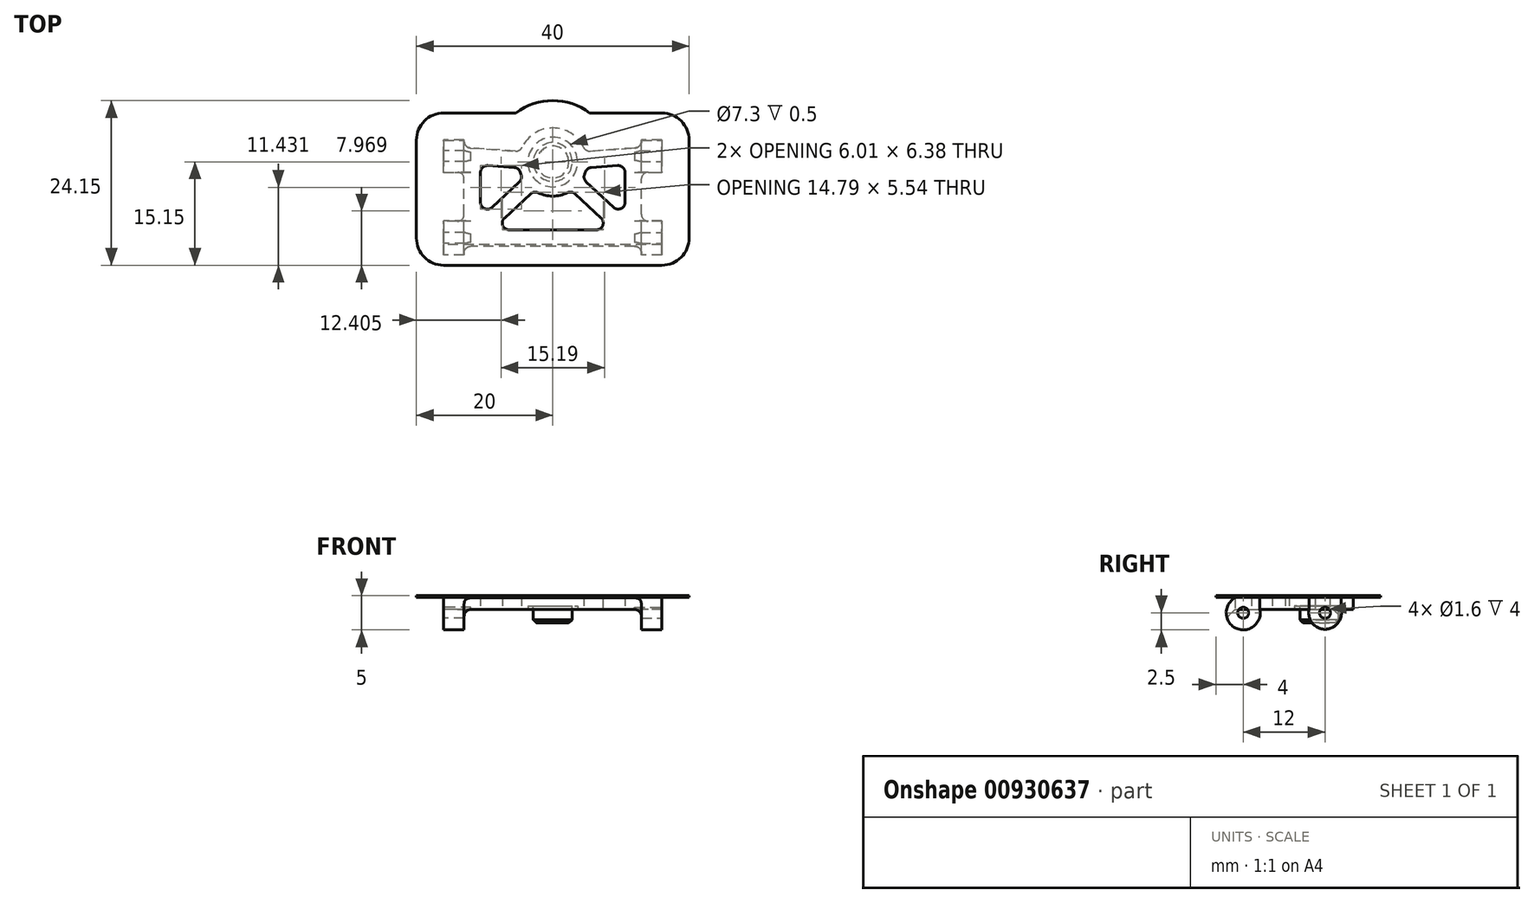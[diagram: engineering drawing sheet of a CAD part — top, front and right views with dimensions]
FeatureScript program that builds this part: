
annotation { "Feature Type Name" : "Feature", "Feature Type Description" : "" }
export const myFeature = defineFeature(function(context is Context, id is Id, definition is map)
    precondition{}
    {
        {
            var Q0;
            Q0=qCreatedBy(makeId("Right.planeOp"),FACE);
            var sketch = newSketch(context, id + "F0", { "sketchPlane" : qUnion([Q0])});
            skArc(sketch, "E0", {"start": v(0, 2.5) * mm, "mid": v(-1.58, -1.94) * mm, "end": v(2.45, 0.5) * mm});
            skArc(sketch, "E1", {"start": v(9.65, 0.5) * mm, "mid": v(12, -2.4) * mm, "end": v(14.35, 0.5) * mm});
            skLineSegment(sketch, "E2", {"start": v(2.45, 0.5) * mm, "end": v(9.65, 0.5) * mm});
            skLineSegment(sketch, "E3", {"start": v(16.35, 2.5) * mm, "end": v(16.35, 0.5) * mm});
            skLineSegment(sketch, "E4", {"start": v(16.35, 0.5) * mm, "end": v(14.35, 0.5) * mm});
            skLineSegment(sketch, "E5", {"start": v(16.35, 2.5) * mm, "end": v(0, 2.5) * mm});
            skSolve(sketch);
        }
        {
            var Q0;
            Q0=qSketchRegion(id+"F0",true);
            extrude(context, id + "F1", {"entities" : qUnion([Q0]), "depth" : 32 * mm, "offsetDistance" : 25 * mm});
        }
        {
            var Q0;
            Q0=makeQuery(id+"F1.opExtrude","SWEPT_FACE",FACE,{"disambiguationData":[OSD([sQuery(id+"F0.wireOp",EDGE,"E3")])]});
            var sketch = newSketch(context, id + "F2", { "sketchPlane" : qUnion([Q0])});
            skLineSegment(sketch, "E6.bottom", {"start": v(-29, 0.5) * mm, "end": v(-3, 0.5) * mm});
            skLineSegment(sketch, "E6.top", {"start": v(-29, -2.5) * mm, "end": v(-3, -2.5) * mm});
            skLineSegment(sketch, "E6.left", {"start": v(-29, 0.5) * mm, "end": v(-29, -2.5) * mm});
            skLineSegment(sketch, "E6.right", {"start": v(-3, 0.5) * mm, "end": v(-3, -2.5) * mm});
            skSolve(sketch);
        }
        {
            var Q0;
            Q0=qSketchRegion(id+"F2",true);
            extrude(context, id + "F3", {"entities" : qUnion([Q0]), "operationType" : NewBodyOperationType.REMOVE, "endBound" : BoundingType.THROUGH_ALL, "oppositeDirection" : true, "depth" : 25 * mm, "offsetDistance" : 25 * mm});
        }
        {
            var Q0;
            Q0=makeQuery(id+"F1.opExtrude","CAP_FACE",FACE,{"disambiguationData":[OSD([sQuery(id+"F0.wireOp",EDGE,"E0"),sQuery(id+"F0.wireOp",EDGE,"E1"),sQuery(id+"F0.wireOp",EDGE,"E2"),sQuery(id+"F0.wireOp",EDGE,"E3"),sQuery(id+"F0.wireOp",EDGE,"E4"),sQuery(id+"F0.wireOp",EDGE,"E5")])],"isStart":false});
            var sketch = newSketch(context, id + "F4", { "sketchPlane" : qUnion([Q0])});
            skCircle(sketch, "E7", {"center": v(0, 0) * mm, "radius": 0.8 * mm});
            skCircle(sketch, "E8", {"center": v(12, 0) * mm, "radius": 0.8 * mm});
            skSolve(sketch);
        }
        {
            var Q0;
            Q0=qSketchRegion(id+"F4",true);
            extrude(context, id + "F5", {"entities" : qUnion([Q0]), "operationType" : NewBodyOperationType.REMOVE, "oppositeDirection" : true, "depth" : 4 * mm, "offsetDistance" : 25 * mm});
        }
        {
            var Q0;
            Q0=makeQuery(id+"F1.opExtrude","CAP_FACE",FACE,{"disambiguationData":[OSD([sQuery(id+"F0.wireOp",EDGE,"E0"),sQuery(id+"F0.wireOp",EDGE,"E1"),sQuery(id+"F0.wireOp",EDGE,"E2"),sQuery(id+"F0.wireOp",EDGE,"E3"),sQuery(id+"F0.wireOp",EDGE,"E4"),sQuery(id+"F0.wireOp",EDGE,"E5")])],"isStart":true});
            var sketch = newSketch(context, id + "F6", { "sketchPlane" : qUnion([Q0])});
            skCircle(sketch, "E9", {"center": v(0, 0) * mm, "radius": 0.8 * mm});
            skCircle(sketch, "E10", {"center": v(-12, 0) * mm, "radius": 0.8 * mm});
            skSolve(sketch);
        }
        {
            var Q0;
            Q0=qSketchRegion(id+"F6",true);
            extrude(context, id + "F7", {"entities" : qUnion([Q0]), "operationType" : NewBodyOperationType.REMOVE, "oppositeDirection" : true, "depth" : 4 * mm, "offsetDistance" : 25 * mm});
        }
        {
            var Q0;
            Q0=makeQuery(id+"F3.boolean.opBoolean","MERGE",FACE,{"derivedFrom":[makeQuery(id+"F1.opExtrude","SWEPT_FACE",FACE,{"disambiguationData":[OSD([sQuery(id+"F0.wireOp",EDGE,"E2")])]}),makeQuery(id+"F1.opExtrude","SWEPT_FACE",FACE,{"disambiguationData":[OSD([sQuery(id+"F0.wireOp",EDGE,"E4")])]}),makeQuery(id+"F3.opExtrude","SWEPT_FACE",FACE,{"disambiguationData":[OSD([sQuery(id+"F2.wireOp",EDGE,"E6.bottom")])]})]});
            var sketch = newSketch(context, id + "F8", { "sketchPlane" : qUnion([Q0])});
            skLineSegment(sketch, "E11", {"start": v(16, 2.45) * mm, "end": v(16, -16.35) * mm, "construction": true});
            skCircle(sketch, "E12", {"center": v(16, -11.15) * mm, "radius": 2.85 * mm});
            skSolve(sketch);
        }
        {
            var Q0;
            Q0=qSketchRegion(id+"F8",true);
            extrude(context, id + "F9", {"entities" : qUnion([Q0]), "operationType" : NewBodyOperationType.ADD, "depth" : 2 * mm, "offsetDistance" : 25 * mm});
        }
        {
            var Q0;
            Q0=makeQuery(id+"F3.boolean.opBoolean","MERGE",FACE,{"derivedFrom":[makeQuery(id+"F1.opExtrude","SWEPT_FACE",FACE,{"disambiguationData":[OSD([sQuery(id+"F0.wireOp",EDGE,"E2")])]}),makeQuery(id+"F1.opExtrude","SWEPT_FACE",FACE,{"disambiguationData":[OSD([sQuery(id+"F0.wireOp",EDGE,"E4")])]}),makeQuery(id+"F3.opExtrude","SWEPT_FACE",FACE,{"disambiguationData":[OSD([sQuery(id+"F2.wireOp",EDGE,"E6.bottom")])]})]});
            var sketch = newSketch(context, id + "F10", { "sketchPlane" : qUnion([Q0])});
            skArc(sketch, "E13", {"start": v(18.74, -6.97) * mm, "mid": v(16, -6.15) * mm, "end": v(13.26, -6.97) * mm});
            skLineSegment(sketch, "E14.bottom", {"start": v(0, -2.45) * mm, "end": v(3, -2.45) * mm});
            skLineSegment(sketch, "E14.top", {"start": v(0, -9.65) * mm, "end": v(3, -9.65) * mm});
            skLineSegment(sketch, "E14.left", {"start": v(0, -2.45) * mm, "end": v(0, -9.65) * mm});
            skLineSegment(sketch, "E14.right", {"start": v(3, -2.45) * mm, "end": v(3, -9.65) * mm});
            skLineSegment(sketch, "E15.bottom", {"start": v(29, -2.45) * mm, "end": v(32, -2.45) * mm});
            skLineSegment(sketch, "E15.top", {"start": v(29, -9.65) * mm, "end": v(32, -9.65) * mm});
            skLineSegment(sketch, "E15.left", {"start": v(29, -2.45) * mm, "end": v(29, -9.65) * mm});
            skLineSegment(sketch, "E15.right", {"start": v(32, -2.45) * mm, "end": v(32, -9.65) * mm});
            skLineSegment(sketch, "E16.bottom", {"start": v(0, -14.35) * mm, "end": v(3, -14.35) * mm});
            skLineSegment(sketch, "E16.left", {"start": v(0, -14.35) * mm, "end": v(0, -16.35) * mm});
            skLineSegment(sketch, "E17.bottom", {"start": v(29, -14.35) * mm, "end": v(32, -14.35) * mm});
            skLineSegment(sketch, "E17.right", {"start": v(32, -14.35) * mm, "end": v(32, -16.35) * mm});
            skLineSegment(sketch, "E18", {"start": v(3, 1.2) * mm, "end": v(29, 1.2) * mm});
            skLineSegment(sketch, "E19", {"start": v(4, 0) * mm, "end": v(28, 0) * mm, "construction": true});
            skLineSegment(sketch, "E20", {"start": v(4, -12) * mm, "end": v(16, -11.15) * mm, "construction": true});
            skLineSegment(sketch, "E21", {"start": v(28, -12) * mm, "end": v(16, -11.15) * mm, "construction": true});
            skLineSegment(sketch, "E22", {"start": v(4, 0) * mm, "end": v(16, -11.15) * mm, "construction": true});
            skLineSegment(sketch, "E23", {"start": v(16, -11.15) * mm, "end": v(28, 0) * mm, "construction": true});
            skLineSegment(sketch, "E24", {"start": v(5.4, -10.7) * mm, "end": v(11.07, -10.3) * mm});
            skLineSegment(sketch, "E25", {"start": v(3, -13.27) * mm, "end": v(11.24, -12.69) * mm});
            skLineSegment(sketch, "E26", {"start": v(26.6, -10.7) * mm, "end": v(20.93, -10.3) * mm});
            skLineSegment(sketch, "E27", {"start": v(29, -13.27) * mm, "end": v(20.76, -12.69) * mm});
            skLineSegment(sketch, "E28", {"start": v(3, -13.27) * mm, "end": v(3, -14.35) * mm});
            skLineSegment(sketch, "E29", {"start": v(29, -13.27) * mm, "end": v(29, -14.35) * mm});
            skLineSegment(sketch, "E30", {"start": v(0, -16.35) * mm, "end": v(16, -16.35) * mm});
            skLineSegment(sketch, "E31", {"start": v(16, -16.35) * mm, "end": v(32, -16.35) * mm});
            skLineSegment(sketch, "E32", {"start": v(7.05, -1.2) * mm, "end": v(13.26, -6.97) * mm});
            skLineSegment(sketch, "E33", {"start": v(24.95, -1.2) * mm, "end": v(18.74, -6.97) * mm});
            skLineSegment(sketch, "E34", {"start": v(5.4, -2.94) * mm, "end": v(11.63, -8.73) * mm});
            skLineSegment(sketch, "E35", {"start": v(26.6, -2.94) * mm, "end": v(20.37, -8.73) * mm});
            skLineSegment(sketch, "E36", {"start": v(5.4, -2.94) * mm, "end": v(5.4, -10.7) * mm});
            skLineSegment(sketch, "E37", {"start": v(26.6, -2.94) * mm, "end": v(26.6, -10.7) * mm});
            skLineSegment(sketch, "E38.trimOffspring", {"start": v(7.05, -1.2) * mm, "end": v(24.95, -1.2) * mm});
            skLineSegment(sketch, "E39", {"start": v(3, 1.2) * mm, "end": v(3, 2.45) * mm});
            skLineSegment(sketch, "E40", {"start": v(3, 2.45) * mm, "end": v(29, 2.45) * mm});
            skLineSegment(sketch, "E41", {"start": v(29, 2.45) * mm, "end": v(29, 1.2) * mm});
            skArc(sketch, "E42.trimOffspring", {"start": v(11.63, -8.73) * mm, "mid": v(11.28, -9.49) * mm, "end": v(11.07, -10.3) * mm});
            skArc(sketch, "E43.trimOffspring", {"start": v(11.24, -12.69) * mm, "mid": v(16, -16.15) * mm, "end": v(20.76, -12.69) * mm});
            skArc(sketch, "E44.trimOffspring", {"start": v(20.93, -10.3) * mm, "mid": v(20.72, -9.49) * mm, "end": v(20.37, -8.73) * mm});
            skPoint(sketch, "E45", {"position": v(28, 0) * mm});
            skSolve(sketch);
        }
        {
            var Q0;
            Q0=qSketchRegion(id+"F10",true);
            extrude(context, id + "F11", {"entities" : qUnion([Q0]), "operationType" : NewBodyOperationType.REMOVE, "endBound" : BoundingType.UP_TO_NEXT, "oppositeDirection" : true, "depth" : 25 * mm, "offsetDistance" : 25 * mm});
        }
        {
            var Q0;
            Q0=makeQuery(id+"F11.boolean.opBoolean","COPY",EDGE,{"derivedFrom":makeQuery(id+"F11.opExtrude","SWEPT_EDGE",EDGE,{"disambiguationData":[OSD([sQuery(id+"F0.wireOp",EDGE,"E1"),sQuery(id+"F0.wireOp",EDGE,"E3"),sQuery(id+"F0.wireOp",EDGE,"E4"),sQuery(id+"F2.wireOp",EDGE,"E6.bottom"),sQuery(id+"F2.wireOp",EDGE,"E6.left"),sQuery(id+"F10.wireOp",EDGE,"E15.top"),sQuery(id+"F10.wireOp",EDGE,"E15.left")])]})});
            var Q1;
            Q1=makeQuery(id+"F11.boolean.opBoolean","COPY",EDGE,{"derivedFrom":makeQuery(id+"F11.opExtrude","SWEPT_EDGE",EDGE,{"disambiguationData":[OSD([sQuery(id+"F0.wireOp",EDGE,"E0"),sQuery(id+"F0.wireOp",EDGE,"E3"),sQuery(id+"F0.wireOp",EDGE,"E4"),sQuery(id+"F2.wireOp",EDGE,"E6.bottom"),sQuery(id+"F2.wireOp",EDGE,"E6.left"),sQuery(id+"F10.wireOp",EDGE,"E15.bottom"),sQuery(id+"F10.wireOp",EDGE,"E15.left")])]})});
            var Q2;
            Q2=makeQuery(id+"F11.boolean.opBoolean","COPY",EDGE,{"derivedFrom":makeQuery(id+"F11.opExtrude","SWEPT_EDGE",EDGE,{"disambiguationData":[OSD([sQuery(id+"F0.wireOp",EDGE,"E0"),sQuery(id+"F0.wireOp",EDGE,"E3"),sQuery(id+"F0.wireOp",EDGE,"E4"),sQuery(id+"F2.wireOp",EDGE,"E6.bottom"),sQuery(id+"F2.wireOp",EDGE,"E6.right"),sQuery(id+"F10.wireOp",EDGE,"E14.bottom"),sQuery(id+"F10.wireOp",EDGE,"E14.right")])]})});
            var Q3;
            Q3=makeQuery(id+"F11.boolean.opBoolean","COPY",EDGE,{"derivedFrom":makeQuery(id+"F11.opExtrude","SWEPT_EDGE",EDGE,{"disambiguationData":[OSD([sQuery(id+"F0.wireOp",EDGE,"E1"),sQuery(id+"F0.wireOp",EDGE,"E3"),sQuery(id+"F0.wireOp",EDGE,"E4"),sQuery(id+"F2.wireOp",EDGE,"E6.bottom"),sQuery(id+"F2.wireOp",EDGE,"E6.right"),sQuery(id+"F10.wireOp",EDGE,"E14.top"),sQuery(id+"F10.wireOp",EDGE,"E14.right")])]})});
            var Q4;
            Q4=makeQuery(id+"F11.boolean.opBoolean","COPY",EDGE,{"derivedFrom":makeQuery(id+"F11.opExtrude","SWEPT_EDGE",EDGE,{"disambiguationData":[OSD([sQuery(id+"F0.wireOp",EDGE,"E3"),sQuery(id+"F0.wireOp",EDGE,"E4"),sQuery(id+"F2.wireOp",EDGE,"E6.bottom"),sQuery(id+"F2.wireOp",EDGE,"E6.left"),sQuery(id+"F10.wireOp",EDGE,"E18"),sQuery(id+"F10.wireOp",EDGE,"E41")])]})});
            var Q5;
            Q5=makeQuery(id+"F11.boolean.opBoolean","COPY",EDGE,{"derivedFrom":makeQuery(id+"F11.opExtrude","SWEPT_EDGE",EDGE,{"disambiguationData":[OSD([sQuery(id+"F0.wireOp",EDGE,"E3"),sQuery(id+"F0.wireOp",EDGE,"E4"),sQuery(id+"F2.wireOp",EDGE,"E6.bottom"),sQuery(id+"F2.wireOp",EDGE,"E6.right"),sQuery(id+"F10.wireOp",EDGE,"E18"),sQuery(id+"F10.wireOp",EDGE,"E39")])]})});
            var Q6;
            Q6=makeQuery(id+"F11.boolean.opBoolean","COPY",EDGE,{"derivedFrom":makeQuery(id+"F11.opExtrude","SWEPT_EDGE",EDGE,{"disambiguationData":[OSD([sQuery(id+"F0.wireOp",EDGE,"E3"),sQuery(id+"F0.wireOp",EDGE,"E4"),sQuery(id+"F2.wireOp",EDGE,"E6.bottom"),sQuery(id+"F2.wireOp",EDGE,"E6.right"),sQuery(id+"F10.wireOp",EDGE,"E25"),sQuery(id+"F10.wireOp",EDGE,"E28")])]})});
            var Q7;
            Q7=makeQuery(id+"F11.boolean.opBoolean","COPY",EDGE,{"derivedFrom":makeQuery(id+"F11.opExtrude","SWEPT_EDGE",EDGE,{"disambiguationData":[OSD([sQuery(id+"F0.wireOp",EDGE,"E3"),sQuery(id+"F0.wireOp",EDGE,"E4"),sQuery(id+"F2.wireOp",EDGE,"E6.bottom"),sQuery(id+"F2.wireOp",EDGE,"E6.left"),sQuery(id+"F10.wireOp",EDGE,"E27"),sQuery(id+"F10.wireOp",EDGE,"E29")])]})});
            fillet(context, id + "F12", {"entities" : qUnion([Q0, Q1, Q2, Q3, Q4, Q5, Q6, Q7]), "radius" : 1 * mm, "tangentPropagation" : true, "allowEdgeOverflow" : false});
        }
        {
            var Q0;
            {var subQ0=makeQuery(id+"F1.opExtrude","SWEPT_FACE",FACE,{"disambiguationData":[OSD([sQuery(id+"F0.wireOp",EDGE,"E2")])]});var subQ1=sQuery(id+"F0.wireOp",EDGE,"E4");var subQ2=makeQuery(id+"F1.opExtrude","SWEPT_FACE",FACE,{"disambiguationData":[OSD([subQ1])]});var subQ3=sQuery(id+"F2.wireOp",EDGE,"E6.bottom");var subQ4=makeQuery(id+"F3.opExtrude","SWEPT_FACE",FACE,{"disambiguationData":[OSD([subQ3])]});var subQ5=makeQuery(id+"F1.opExtrude","SWEPT_FACE",FACE,{"disambiguationData":[OSD([sQuery(id+"F0.wireOp",EDGE,"E0")])]});var subQ6=sQuery(id+"F2.wireOp",EDGE,"E6.left");var subQ7=makeQuery(id+"F3.opExtrude","SWEPT_FACE",FACE,{"disambiguationData":[OSD([subQ6])]});Q0=makeQuery(id+"F5.boolean.opBoolean","SPLIT",EDGE,{"disambiguationData":[topologyDisambiguationEdgeConnected([subQ0,subQ2,subQ4,makeQuery(id+"F3.boolean.opBoolean","COPY",FACE,{"disambiguationData":[TD([subQ5])],"derivedFrom":subQ7})]),OD(0.0)],"derivedFrom":makeQuery(id+"F3.boolean.opBoolean","COPY",EDGE,{"disambiguationData":[TD([subQ5])],"derivedFrom":makeQuery(id+"F3.opExtrude","SWEPT_EDGE",EDGE,{"disambiguationData":[OSD([sQuery(id+"F0.wireOp",EDGE,"E3"),subQ1,subQ3,subQ6])]})})});}
            var Q1;
            {var subQ0=makeQuery(id+"F1.opExtrude","SWEPT_FACE",FACE,{"disambiguationData":[OSD([sQuery(id+"F0.wireOp",EDGE,"E2")])]});var subQ1=sQuery(id+"F0.wireOp",EDGE,"E4");var subQ2=makeQuery(id+"F1.opExtrude","SWEPT_FACE",FACE,{"disambiguationData":[OSD([subQ1])]});var subQ3=sQuery(id+"F2.wireOp",EDGE,"E6.bottom");var subQ4=makeQuery(id+"F3.opExtrude","SWEPT_FACE",FACE,{"disambiguationData":[OSD([subQ3])]});var subQ5=makeQuery(id+"F1.opExtrude","SWEPT_FACE",FACE,{"disambiguationData":[OSD([sQuery(id+"F0.wireOp",EDGE,"E0")])]});var subQ6=sQuery(id+"F2.wireOp",EDGE,"E6.left");var subQ7=makeQuery(id+"F3.opExtrude","SWEPT_FACE",FACE,{"disambiguationData":[OSD([subQ6])]});Q1=makeQuery(id+"F5.boolean.opBoolean","SPLIT",EDGE,{"disambiguationData":[topologyDisambiguationEdgeConnected([subQ0,subQ2,subQ4,makeQuery(id+"F3.boolean.opBoolean","COPY",FACE,{"disambiguationData":[TD([subQ5])],"derivedFrom":subQ7})]),OD(1.0)],"derivedFrom":makeQuery(id+"F3.boolean.opBoolean","COPY",EDGE,{"disambiguationData":[TD([subQ5])],"derivedFrom":makeQuery(id+"F3.opExtrude","SWEPT_EDGE",EDGE,{"disambiguationData":[OSD([sQuery(id+"F0.wireOp",EDGE,"E3"),subQ1,subQ3,subQ6])]})})});}
            var Q2;
            {var subQ0=makeQuery(id+"F1.opExtrude","SWEPT_FACE",FACE,{"disambiguationData":[OSD([sQuery(id+"F0.wireOp",EDGE,"E2")])]});var subQ1=sQuery(id+"F0.wireOp",EDGE,"E4");var subQ2=makeQuery(id+"F1.opExtrude","SWEPT_FACE",FACE,{"disambiguationData":[OSD([subQ1])]});var subQ3=sQuery(id+"F2.wireOp",EDGE,"E6.bottom");var subQ4=makeQuery(id+"F3.opExtrude","SWEPT_FACE",FACE,{"disambiguationData":[OSD([subQ3])]});var subQ5=makeQuery(id+"F1.opExtrude","SWEPT_FACE",FACE,{"disambiguationData":[OSD([sQuery(id+"F0.wireOp",EDGE,"E0")])]});var subQ6=sQuery(id+"F2.wireOp",EDGE,"E6.right");var subQ7=makeQuery(id+"F3.opExtrude","SWEPT_FACE",FACE,{"disambiguationData":[OSD([subQ6])]});Q2=makeQuery(id+"F7.boolean.opBoolean","SPLIT",EDGE,{"disambiguationData":[topologyDisambiguationEdgeConnected([subQ0,subQ2,subQ4,makeQuery(id+"F3.boolean.opBoolean","COPY",FACE,{"disambiguationData":[TD([subQ5])],"derivedFrom":subQ7})]),OD(1.0)],"derivedFrom":makeQuery(id+"F3.boolean.opBoolean","COPY",EDGE,{"disambiguationData":[TD([subQ5])],"derivedFrom":makeQuery(id+"F3.opExtrude","SWEPT_EDGE",EDGE,{"disambiguationData":[OSD([sQuery(id+"F0.wireOp",EDGE,"E3"),subQ1,subQ3,subQ6])]})})});}
            var Q3;
            {var subQ0=makeQuery(id+"F1.opExtrude","SWEPT_FACE",FACE,{"disambiguationData":[OSD([sQuery(id+"F0.wireOp",EDGE,"E2")])]});var subQ1=sQuery(id+"F0.wireOp",EDGE,"E4");var subQ2=makeQuery(id+"F1.opExtrude","SWEPT_FACE",FACE,{"disambiguationData":[OSD([subQ1])]});var subQ3=sQuery(id+"F2.wireOp",EDGE,"E6.bottom");var subQ4=makeQuery(id+"F3.opExtrude","SWEPT_FACE",FACE,{"disambiguationData":[OSD([subQ3])]});var subQ5=makeQuery(id+"F1.opExtrude","SWEPT_FACE",FACE,{"disambiguationData":[OSD([sQuery(id+"F0.wireOp",EDGE,"E0")])]});var subQ6=sQuery(id+"F2.wireOp",EDGE,"E6.right");var subQ7=makeQuery(id+"F3.opExtrude","SWEPT_FACE",FACE,{"disambiguationData":[OSD([subQ6])]});Q3=makeQuery(id+"F7.boolean.opBoolean","SPLIT",EDGE,{"disambiguationData":[topologyDisambiguationEdgeConnected([subQ0,subQ2,subQ4,makeQuery(id+"F3.boolean.opBoolean","COPY",FACE,{"disambiguationData":[TD([subQ5])],"derivedFrom":subQ7})]),OD(0.0)],"derivedFrom":makeQuery(id+"F3.boolean.opBoolean","COPY",EDGE,{"disambiguationData":[TD([subQ5])],"derivedFrom":makeQuery(id+"F3.opExtrude","SWEPT_EDGE",EDGE,{"disambiguationData":[OSD([sQuery(id+"F0.wireOp",EDGE,"E3"),subQ1,subQ3,subQ6])]})})});}
            var Q4;
            {var subQ0=makeQuery(id+"F1.opExtrude","SWEPT_FACE",FACE,{"disambiguationData":[OSD([sQuery(id+"F0.wireOp",EDGE,"E2")])]});var subQ1=sQuery(id+"F0.wireOp",EDGE,"E4");var subQ2=makeQuery(id+"F1.opExtrude","SWEPT_FACE",FACE,{"disambiguationData":[OSD([subQ1])]});var subQ3=makeQuery(id+"F1.opExtrude","SWEPT_FACE",FACE,{"disambiguationData":[OSD([sQuery(id+"F0.wireOp",EDGE,"E1")])]});var subQ4=sQuery(id+"F2.wireOp",EDGE,"E6.bottom");var subQ5=makeQuery(id+"F3.opExtrude","SWEPT_FACE",FACE,{"disambiguationData":[OSD([subQ4])]});var subQ6=sQuery(id+"F2.wireOp",EDGE,"E6.right");var subQ7=makeQuery(id+"F3.opExtrude","SWEPT_FACE",FACE,{"disambiguationData":[OSD([subQ6])]});Q4=makeQuery(id+"F7.boolean.opBoolean","SPLIT",EDGE,{"disambiguationData":[topologyDisambiguationEdgeConnected([subQ0,subQ2,subQ5,makeQuery(id+"F3.boolean.opBoolean","COPY",FACE,{"disambiguationData":[TD([subQ3])],"derivedFrom":subQ7})]),OD(0.0)],"derivedFrom":makeQuery(id+"F3.boolean.opBoolean","COPY",EDGE,{"disambiguationData":[TD([subQ3])],"derivedFrom":makeQuery(id+"F3.opExtrude","SWEPT_EDGE",EDGE,{"disambiguationData":[OSD([sQuery(id+"F0.wireOp",EDGE,"E3"),subQ1,subQ4,subQ6])]})})});}
            var Q5;
            {var subQ0=makeQuery(id+"F1.opExtrude","SWEPT_FACE",FACE,{"disambiguationData":[OSD([sQuery(id+"F0.wireOp",EDGE,"E2")])]});var subQ1=sQuery(id+"F0.wireOp",EDGE,"E4");var subQ2=makeQuery(id+"F1.opExtrude","SWEPT_FACE",FACE,{"disambiguationData":[OSD([subQ1])]});var subQ3=makeQuery(id+"F1.opExtrude","SWEPT_FACE",FACE,{"disambiguationData":[OSD([sQuery(id+"F0.wireOp",EDGE,"E1")])]});var subQ4=sQuery(id+"F2.wireOp",EDGE,"E6.bottom");var subQ5=makeQuery(id+"F3.opExtrude","SWEPT_FACE",FACE,{"disambiguationData":[OSD([subQ4])]});var subQ6=sQuery(id+"F2.wireOp",EDGE,"E6.right");var subQ7=makeQuery(id+"F3.opExtrude","SWEPT_FACE",FACE,{"disambiguationData":[OSD([subQ6])]});Q5=makeQuery(id+"F7.boolean.opBoolean","SPLIT",EDGE,{"disambiguationData":[topologyDisambiguationEdgeConnected([subQ0,subQ2,subQ5,makeQuery(id+"F3.boolean.opBoolean","COPY",FACE,{"disambiguationData":[TD([subQ3])],"derivedFrom":subQ7})]),OD(1.0)],"derivedFrom":makeQuery(id+"F3.boolean.opBoolean","COPY",EDGE,{"disambiguationData":[TD([subQ3])],"derivedFrom":makeQuery(id+"F3.opExtrude","SWEPT_EDGE",EDGE,{"disambiguationData":[OSD([sQuery(id+"F0.wireOp",EDGE,"E3"),subQ1,subQ4,subQ6])]})})});}
            var Q6;
            {var subQ0=makeQuery(id+"F1.opExtrude","SWEPT_FACE",FACE,{"disambiguationData":[OSD([sQuery(id+"F0.wireOp",EDGE,"E2")])]});var subQ1=makeQuery(id+"F1.opExtrude","SWEPT_FACE",FACE,{"disambiguationData":[OSD([sQuery(id+"F0.wireOp",EDGE,"E1")])]});var subQ2=sQuery(id+"F2.wireOp",EDGE,"E6.bottom");var subQ3=makeQuery(id+"F3.opExtrude","SWEPT_FACE",FACE,{"disambiguationData":[OSD([subQ2])]});var subQ4=sQuery(id+"F0.wireOp",EDGE,"E4");var subQ5=makeQuery(id+"F1.opExtrude","SWEPT_FACE",FACE,{"disambiguationData":[OSD([subQ4])]});var subQ6=sQuery(id+"F2.wireOp",EDGE,"E6.left");var subQ7=makeQuery(id+"F3.opExtrude","SWEPT_FACE",FACE,{"disambiguationData":[OSD([subQ6])]});Q6=makeQuery(id+"F5.boolean.opBoolean","SPLIT",EDGE,{"disambiguationData":[topologyDisambiguationEdgeConnected([subQ0,subQ5,subQ3,makeQuery(id+"F3.boolean.opBoolean","COPY",FACE,{"disambiguationData":[TD([subQ1])],"derivedFrom":subQ7})]),OD(0.0)],"derivedFrom":makeQuery(id+"F3.boolean.opBoolean","COPY",EDGE,{"disambiguationData":[TD([subQ1])],"derivedFrom":makeQuery(id+"F3.opExtrude","SWEPT_EDGE",EDGE,{"disambiguationData":[OSD([sQuery(id+"F0.wireOp",EDGE,"E3"),subQ4,subQ2,subQ6])]})})});}
            var Q7;
            {var subQ0=makeQuery(id+"F1.opExtrude","SWEPT_FACE",FACE,{"disambiguationData":[OSD([sQuery(id+"F0.wireOp",EDGE,"E2")])]});var subQ1=makeQuery(id+"F1.opExtrude","SWEPT_FACE",FACE,{"disambiguationData":[OSD([sQuery(id+"F0.wireOp",EDGE,"E1")])]});var subQ2=sQuery(id+"F2.wireOp",EDGE,"E6.bottom");var subQ3=makeQuery(id+"F3.opExtrude","SWEPT_FACE",FACE,{"disambiguationData":[OSD([subQ2])]});var subQ4=sQuery(id+"F0.wireOp",EDGE,"E4");var subQ5=makeQuery(id+"F1.opExtrude","SWEPT_FACE",FACE,{"disambiguationData":[OSD([subQ4])]});var subQ6=sQuery(id+"F2.wireOp",EDGE,"E6.left");var subQ7=makeQuery(id+"F3.opExtrude","SWEPT_FACE",FACE,{"disambiguationData":[OSD([subQ6])]});Q7=makeQuery(id+"F5.boolean.opBoolean","SPLIT",EDGE,{"disambiguationData":[topologyDisambiguationEdgeConnected([subQ0,subQ5,subQ3,makeQuery(id+"F3.boolean.opBoolean","COPY",FACE,{"disambiguationData":[TD([subQ1])],"derivedFrom":subQ7})]),OD(1.0)],"derivedFrom":makeQuery(id+"F3.boolean.opBoolean","COPY",EDGE,{"disambiguationData":[TD([subQ1])],"derivedFrom":makeQuery(id+"F3.opExtrude","SWEPT_EDGE",EDGE,{"disambiguationData":[OSD([sQuery(id+"F0.wireOp",EDGE,"E3"),subQ4,subQ2,subQ6])]})})});}
            fillet(context, id + "F13", {"entities" : qUnion([Q0, Q1, Q2, Q3, Q4, Q5, Q6, Q7]), "radius" : 1 * mm, "tangentPropagation" : true, "allowEdgeOverflow" : false});
        }
        {
            var Q0;
            Q0=makeQuery(id+"F3.boolean.opBoolean","MERGE",FACE,{"derivedFrom":[makeQuery(id+"F1.opExtrude","SWEPT_FACE",FACE,{"disambiguationData":[OSD([sQuery(id+"F0.wireOp",EDGE,"E2")])]}),makeQuery(id+"F1.opExtrude","SWEPT_FACE",FACE,{"disambiguationData":[OSD([sQuery(id+"F0.wireOp",EDGE,"E4")])]}),makeQuery(id+"F3.opExtrude","SWEPT_FACE",FACE,{"disambiguationData":[OSD([sQuery(id+"F2.wireOp",EDGE,"E6.bottom")])]})]});
            var sketch = newSketch(context, id + "F14", { "sketchPlane" : qUnion([Q0])});
            skCircle(sketch, "E46", {"center": v(16, -11.15) * mm, "radius": 3.65 * mm});
            skCircle(sketch, "E47", {"center": v(16, -11.15) * mm, "radius": 2.85 * mm});
            skSolve(sketch);
        }
        {
            var Q0;
            Q0=qSketchRegion(id+"F14",true);
            extrude(context, id + "F15", {"entities" : qUnion([Q0]), "operationType" : NewBodyOperationType.REMOVE, "oppositeDirection" : true, "depth" : 0.5 * mm, "offsetDistance" : 25 * mm});
        }
        {
            var Q0;
            Q0=makeQuery(id+"F11.boolean.opBoolean","COPY",EDGE,{"derivedFrom":makeQuery(id+"F11.opExtrude","SWEPT_EDGE",EDGE,{"disambiguationData":[OSD([sQuery(id+"F10.wireOp",EDGE,"E25"),sQuery(id+"F10.wireOp",EDGE,"E43.trimOffspring")])]})});
            var Q1;
            Q1=makeQuery(id+"F11.boolean.opBoolean","COPY",EDGE,{"derivedFrom":makeQuery(id+"F11.opExtrude","SWEPT_EDGE",EDGE,{"disambiguationData":[OSD([sQuery(id+"F10.wireOp",EDGE,"E27"),sQuery(id+"F10.wireOp",EDGE,"E43.trimOffspring")])]})});
            var Q2;
            Q2=makeQuery(id+"F11.boolean.opBoolean","COPY",EDGE,{"derivedFrom":makeQuery(id+"F11.opExtrude","SWEPT_EDGE",EDGE,{"disambiguationData":[OSD([sQuery(id+"F10.wireOp",EDGE,"E26"),sQuery(id+"F10.wireOp",EDGE,"E37")])]})});
            var Q3;
            Q3=makeQuery(id+"F11.boolean.opBoolean","COPY",EDGE,{"derivedFrom":makeQuery(id+"F11.opExtrude","SWEPT_EDGE",EDGE,{"disambiguationData":[OSD([sQuery(id+"F10.wireOp",EDGE,"E35"),sQuery(id+"F10.wireOp",EDGE,"E37")])]})});
            var Q4;
            Q4=makeQuery(id+"F11.boolean.opBoolean","COPY",EDGE,{"derivedFrom":makeQuery(id+"F11.opExtrude","SWEPT_EDGE",EDGE,{"disambiguationData":[OSD([sQuery(id+"F10.wireOp",EDGE,"E33"),sQuery(id+"F10.wireOp",EDGE,"E38.trimOffspring")])]})});
            var Q5;
            Q5=makeQuery(id+"F11.boolean.opBoolean","COPY",EDGE,{"derivedFrom":makeQuery(id+"F11.opExtrude","SWEPT_EDGE",EDGE,{"disambiguationData":[OSD([sQuery(id+"F10.wireOp",EDGE,"E13"),sQuery(id+"F10.wireOp",EDGE,"E33")])]})});
            var Q6;
            Q6=makeQuery(id+"F11.boolean.opBoolean","COPY",EDGE,{"derivedFrom":makeQuery(id+"F11.opExtrude","SWEPT_EDGE",EDGE,{"disambiguationData":[OSD([sQuery(id+"F10.wireOp",EDGE,"E35"),sQuery(id+"F10.wireOp",EDGE,"E44.trimOffspring")])]})});
            var Q7;
            Q7=makeQuery(id+"F11.boolean.opBoolean","COPY",EDGE,{"derivedFrom":makeQuery(id+"F11.opExtrude","SWEPT_EDGE",EDGE,{"disambiguationData":[OSD([sQuery(id+"F10.wireOp",EDGE,"E26"),sQuery(id+"F10.wireOp",EDGE,"E44.trimOffspring")])]})});
            var Q8;
            Q8=makeQuery(id+"F11.boolean.opBoolean","COPY",EDGE,{"derivedFrom":makeQuery(id+"F11.opExtrude","SWEPT_EDGE",EDGE,{"disambiguationData":[OSD([sQuery(id+"F10.wireOp",EDGE,"E32"),sQuery(id+"F10.wireOp",EDGE,"E38.trimOffspring")])]})});
            var Q9;
            Q9=makeQuery(id+"F11.boolean.opBoolean","COPY",EDGE,{"derivedFrom":makeQuery(id+"F11.opExtrude","SWEPT_EDGE",EDGE,{"disambiguationData":[OSD([sQuery(id+"F10.wireOp",EDGE,"E13"),sQuery(id+"F10.wireOp",EDGE,"E32")])]})});
            var Q10;
            Q10=makeQuery(id+"F11.boolean.opBoolean","COPY",EDGE,{"derivedFrom":makeQuery(id+"F11.opExtrude","SWEPT_EDGE",EDGE,{"disambiguationData":[OSD([sQuery(id+"F10.wireOp",EDGE,"E34"),sQuery(id+"F10.wireOp",EDGE,"E36")])]})});
            var Q11;
            Q11=makeQuery(id+"F11.boolean.opBoolean","COPY",EDGE,{"derivedFrom":makeQuery(id+"F11.opExtrude","SWEPT_EDGE",EDGE,{"disambiguationData":[OSD([sQuery(id+"F10.wireOp",EDGE,"E34"),sQuery(id+"F10.wireOp",EDGE,"E42.trimOffspring")])]})});
            var Q12;
            Q12=makeQuery(id+"F11.boolean.opBoolean","COPY",EDGE,{"derivedFrom":makeQuery(id+"F11.opExtrude","SWEPT_EDGE",EDGE,{"disambiguationData":[OSD([sQuery(id+"F10.wireOp",EDGE,"E24"),sQuery(id+"F10.wireOp",EDGE,"E42.trimOffspring")])]})});
            var Q13;
            Q13=makeQuery(id+"F11.boolean.opBoolean","COPY",EDGE,{"derivedFrom":makeQuery(id+"F11.opExtrude","SWEPT_EDGE",EDGE,{"disambiguationData":[OSD([sQuery(id+"F10.wireOp",EDGE,"E24"),sQuery(id+"F10.wireOp",EDGE,"E36")])]})});
            fillet(context, id + "F16", {"entities" : qUnion([Q0, Q1, Q2, Q3, Q4, Q5, Q6, Q7, Q8, Q9, Q10, Q11, Q12, Q13]), "radius" : 1 * mm, "tangentPropagation" : true, "allowEdgeOverflow" : false});
        }
        {
            var Q0;
            Q0=makeQuery(id+"F9.opExtrude","CAP_EDGE",EDGE,{"disambiguationData":[OSD([sQuery(id+"F8.wireOp",EDGE,"E12")])],"isStart":false});
            chamfer(context, id + "F17", {"entities" : qUnion([Q0]), "width" : 0.5 * mm, "tangentPropagation" : true});
        }
        {
            var Q0;
            Q0=makeQuery(id+"F1.opExtrude","SWEPT_FACE",FACE,{"disambiguationData":[OSD([sQuery(id+"F0.wireOp",EDGE,"E5")])]});
            var sketch = newSketch(context, id + "F18", { "sketchPlane" : qUnion([Q0])});
            skLineSegment(sketch, "E48.bottom", {"start": v(0, 18.35) * mm, "end": v(10.6, 18.35) * mm});
            skLineSegment(sketch, "E48.top", {"start": v(0, -4) * mm, "end": v(32, -4) * mm});
            skLineSegment(sketch, "E48.left", {"start": v(-4, 14.35) * mm, "end": v(-4, 0) * mm});
            skLineSegment(sketch, "E48.right", {"start": v(36, 14.35) * mm, "end": v(36, 0) * mm});
            skArc(sketch, "E49", {"start": v(0, 18.35) * mm, "mid": v(-2.83, 17.18) * mm, "end": v(-4, 14.35) * mm});
            skArc(sketch, "E50", {"start": v(36, 14.35) * mm, "mid": v(34.83, 17.18) * mm, "end": v(32, 18.35) * mm});
            skArc(sketch, "E51", {"start": v(-4, 0) * mm, "mid": v(-2.83, -2.83) * mm, "end": v(0, -4) * mm});
            skArc(sketch, "E52", {"start": v(21.4, 18.35) * mm, "mid": v(16, 20.15) * mm, "end": v(10.6, 18.35) * mm});
            skLineSegment(sketch, "E53.trimOffspring", {"start": v(21.4, 18.35) * mm, "end": v(32, 18.35) * mm});
            skArc(sketch, "E54", {"start": v(32, -4) * mm, "mid": v(34.83, -2.83) * mm, "end": v(36, 0) * mm});
            skLineSegment(sketch, "E55", {"start": v(0, 14.35) * mm, "end": v(0, 9.65) * mm});
            skLineSegment(sketch, "E56", {"start": v(0, 9.65) * mm, "end": v(2, 9.65) * mm});
            skLineSegment(sketch, "E57", {"start": v(0, 14.35) * mm, "end": v(3, 14.35) * mm});
            skLineSegment(sketch, "E58", {"start": v(3.93, 13.2) * mm, "end": v(10.52, 12.74) * mm});
            skLineSegment(sketch, "E59", {"start": v(21.48, 12.74) * mm, "end": v(28.07, 13.2) * mm});
            skLineSegment(sketch, "E60", {"start": v(29, 14.35) * mm, "end": v(32, 14.35) * mm});
            skLineSegment(sketch, "E61", {"start": v(32, 14.35) * mm, "end": v(32, 9.65) * mm});
            skLineSegment(sketch, "E62", {"start": v(32, 9.65) * mm, "end": v(30, 9.65) * mm});
            skLineSegment(sketch, "E63", {"start": v(29, 8.65) * mm, "end": v(29, 3.45) * mm});
            skLineSegment(sketch, "E64", {"start": v(30, 2.45) * mm, "end": v(32, 2.45) * mm});
            skLineSegment(sketch, "E65", {"start": v(32, 2.45) * mm, "end": v(32, 0) * mm});
            skLineSegment(sketch, "E66", {"start": v(32, 0) * mm, "end": v(0, 0) * mm});
            skLineSegment(sketch, "E67", {"start": v(0, 0) * mm, "end": v(0, 2.45) * mm});
            skLineSegment(sketch, "E68", {"start": v(0, 2.45) * mm, "end": v(2, 2.45) * mm});
            skLineSegment(sketch, "E69", {"start": v(3, 8.65) * mm, "end": v(3, 3.45) * mm});
            skArc(sketch, "E70", {"start": v(3, 14.35) * mm, "mid": v(3.22, 13.58) * mm, "end": v(3.93, 13.2) * mm});
            skArc(sketch, "E71", {"start": v(10.52, 12.74) * mm, "mid": v(11.1, 12.87) * mm, "end": v(11.49, 13.3) * mm});
            skArc(sketch, "E72", {"start": v(20.51, 13.3) * mm, "mid": v(16, 16.15) * mm, "end": v(11.49, 13.3) * mm});
            skArc(sketch, "E73", {"start": v(20.51, 13.3) * mm, "mid": v(20.9, 12.87) * mm, "end": v(21.48, 12.74) * mm});
            skArc(sketch, "E74", {"start": v(28.07, 13.2) * mm, "mid": v(28.78, 13.58) * mm, "end": v(29, 14.35) * mm});
            skArc(sketch, "E75", {"start": v(30, 9.65) * mm, "mid": v(29.3, 9.36) * mm, "end": v(29, 8.65) * mm});
            skArc(sketch, "E76", {"start": v(29, 3.45) * mm, "mid": v(29.3, 2.74) * mm, "end": v(30, 2.45) * mm});
            skArc(sketch, "E77", {"start": v(2, 2.45) * mm, "mid": v(2.7, 2.74) * mm, "end": v(3, 3.45) * mm});
            skArc(sketch, "E78", {"start": v(3, 8.65) * mm, "mid": v(2.7, 9.36) * mm, "end": v(2, 9.65) * mm});
            skSolve(sketch);
        }
        {
            var Q0;
            Q0=qSketchRegion(id+"F18",true);
            extrude(context, id + "F19", {"entities" : qUnion([Q0]), "operationType" : NewBodyOperationType.ADD, "oppositeDirection" : true, "depth" : 0.2 * mm, "offsetDistance" : 25 * mm});
        }
    });
